# Revit family: WWW_A3-WTI-Flat-Arch-0966-FAA2
name_source: partatom
category: Windows
revit_build: Autodesk Revit 2016 (Build: 20150220_1215(x64)
units: mm (PartAtom-declared; Revit-internal decimal feet)

## family parameters
Always vertical = Yes
Cut with Voids When Loaded = No
Host = Wall
Room Calculation Point = No
Shared = No

## types (2) — shared parameters
Assembly Code = B2020130
Default Sill Height = 1334 mm  [stored 4.37664 ft]
Frame Material = Wood- Timber
Head Height = 2300 mm
Height = 966 mm
Manufacturer = AC Shopfitters (Windows)
Manufacturer Code = FAA2
Model = Flat Arch
Type Comments = Series iv Frame Profile
URL = www.acdoors.co.za
Wall Closure = By host

## per-type parameters (varying)
| type | Width |
| 0966 x 0580 FAA2 | 580 mm  [stored 1.90289 ft] |
| 0966 x 1116 FAA2 | 1116 mm |

note: [stored X ft] marks values corroborated as IEEE doubles in the binary element streams (Revit-internal decimal feet)

## geometry (parser evidence)
native form markers: Sweep x7
no freeform markers — native parametric forms only
